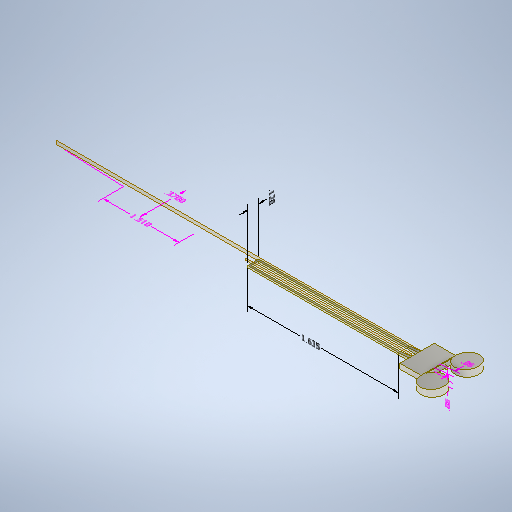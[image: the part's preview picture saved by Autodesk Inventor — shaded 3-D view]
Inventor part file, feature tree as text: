
AUTODESK INVENTOR PART (.ipt)
format: ipt  version: 2025.3 (Build 293356030, 356C)  size: 354,304 bytes
history: native  units: in
note: dims shown in document units (in); Inventor stores cm internally (conversion verified against a paired STEP export)
features: other x8, sketch x5, plane x4, extrude x2, sweep x1, loft x1, mirror x1
ambient origin geometry x8: Origin, YZ Plane, XZ Plane, XY Plane, X Axis, Y Axis, Z Axis, Center Point
bodies: Solid1 (feature_tree)
feature tree (22):
  other  "Annotations"
  sweep  "Sweep1"
  plane  "Work Plane1"
  plane  "Work Plane2"
  plane  "Work Plane4"
  sketch  "Sketch15"  dims[d86=-0.1175in d89=0.1in]
  loft  "Loft3"
  plane  "Work Plane5"
  mirror  "Mirror3"
  extrude  "Extrusion9"  Depth=0.1in
  extrude  "Extrusion10"  TaperAngle=0.0deg  [1 undecoded]
  sketch  "Sketch1"  dims[d6=0.0in d7=0.0in d11=0.375in d19=-0.25in]
  sketch  "Sketch2"  dims[d69=1.625in d70=1.625in]
  other  "Edges4"
  sketch  "Sketch17"  dims[d90=0.0in d91=0.0in]
  sketch  "Sketch18"  dims[d92=0.0in d98=0.02in d99=0.02in d100=0.055in d102=0.055in d104=0.0in d109=0.0in d110=90.0deg d111=0.0in d112=90.0deg d116=-0.06in d127=0.25in d128=0.25in d129=0.375in d132=0.04in d134=0.1875in d135=0.25in d136=0.0in d137=0.23in d138=0.0in d113=0.0in d114=0.3937in d115=0.12in d120=0.0in d121=0.3937in d122=0.055in d123=0.0in d124=0.3937in d125=0.055in d126=1.635in d42=0.2341in d43=0.169in d44=0.37in d48=0.2141in d49=0.2512in d50=1.51in]
  other  "Linear Dimension 1"
  other  "Linear Dimension 3"
  other  "Linear Dimension 4"
  other  "Linear Dimension 6"
  other  "Linear Dimension 7"
  other  "Linear Dimension 8"
note: 1 required parameter value undecoded (feature->parameter linkage not recoverable at this tier; creation-order binding heuristic only, values carry confidence <= 0.55)
